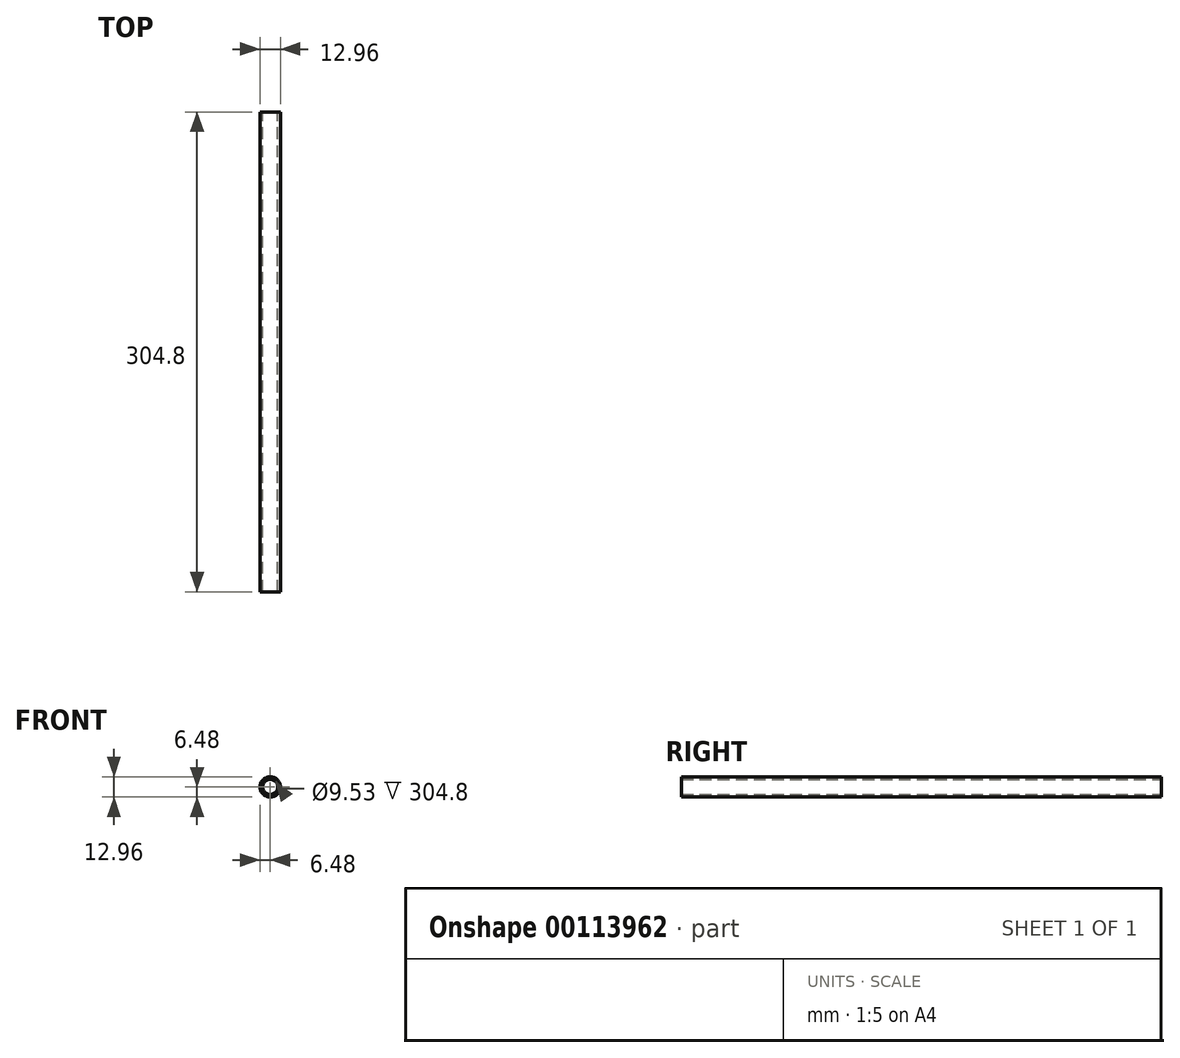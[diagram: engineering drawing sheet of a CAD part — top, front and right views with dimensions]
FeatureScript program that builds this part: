
annotation { "Feature Type Name" : "Feature", "Feature Type Description" : "" }
export const myFeature = defineFeature(function(context is Context, id is Id, definition is map)
    precondition{}
    {
        {
            var Q0;
            Q0=qCreatedBy(makeId("Front.planeOp"),FACE);
            var sketch = newSketch(context, id + "F0", { "sketchPlane" : qUnion([Q0])});
            skCircle(sketch, "E0", {"center": v(0, 0) * mm, "radius": 6.48 * mm});
            skCircle(sketch, "E1", {"center": v(0, 0) * mm, "radius": 4.76 * mm});
            skSolve(sketch);
        }
        {
            var Q0;
            Q0=makeQuery(id+"F0.imprint","IMPRINT",FACE,{"disambiguationData":[TD([[makeQuery(id+"F0.imprint","IMPRINT",EDGE,{"derivedFrom":sQuery(id+"F0.wireOp",EDGE,"E0")}),1.0]])]});
            extrude(context, id + "F1", {"entities" : qUnion([Q0]), "depth" : 304.8 * mm});
        }
    });
